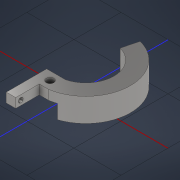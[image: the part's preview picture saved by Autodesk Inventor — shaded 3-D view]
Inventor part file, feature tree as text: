
AUTODESK INVENTOR PART (.ipt)
format: ipt  version: 2021 (Build 250183000, 183)  size: 168,448 bytes
history: native  units: mm
features: sketch x5, extrude x4, other x3, hole x2, projected_geometry x1
ambient origin geometry x8: Origin, YZ Plane, XZ Plane, XY Plane, X Axis, Y Axis, Z Axis, Center Point
bodies: Solid1 (feature_tree)
feature tree (15):
  extrude  "clamp"  Depth=7.0mm
  other  "reduction"
  other  "reductionSplit"
  extrude  "arm_c"  Depth=5.0mm
  extrude  "arb_b"  Depth=10.0mm TaperAngle=0.0deg
  hole  "pinHole"  [1 undecoded]
  extrude  "halfcut"  Depth=4.0mm TaperAngle=0.0deg
  hole  "cableHole"  [1 undecoded]
  other  "clawBase"
  sketch  "Sketch7"  dims[d3=12.0mm d5=7.0mm]
  projected_geometry  "Projected Loop2"
  sketch  "Sketch8"  dims[d6=0.0mm d7=5.0mm]
  sketch  "Sketch9"  dims[d8=3.0mm d9=10.0mm d10=0.0mm]
  sketch  "Sketch10"  dims[d11=12.0mm d12=0.0mm]
  sketch  "Sketch11"  dims[d14=-3.0mm d33=8.0mm d34=0.0mm d35=4.0mm d36=10.0mm d37=0.0mm d39=7.142713mm d41=0.0mm d42=3.571357mm d43=3.25mm d44=6.0mm d45=4.0mm d46=2.0mm d47=90.0deg d48=8.0mm d49=0.0mm d50=6.0mm d51=4.25mm d52=0.0mm d54=2.0mm d55=4.0mm d56=2.137935mm d57=2.0mm d58=6.0mm d59=4.0mm d60=2.0mm d61=90.0deg d62=8.0mm d63=0.0mm d64=3.0mm d65=0.0mm d66=19.75mm d67=0.0mm d15=0.872665mm d16=0.5mm d17=0.872665mm d68=0.5mm d69=0.872665mm d70=0.5mm d71=0.872665mm]
note: 2 required parameter values undecoded (feature->parameter linkage not recoverable at this tier; creation-order binding heuristic only, values carry confidence <= 0.55)
